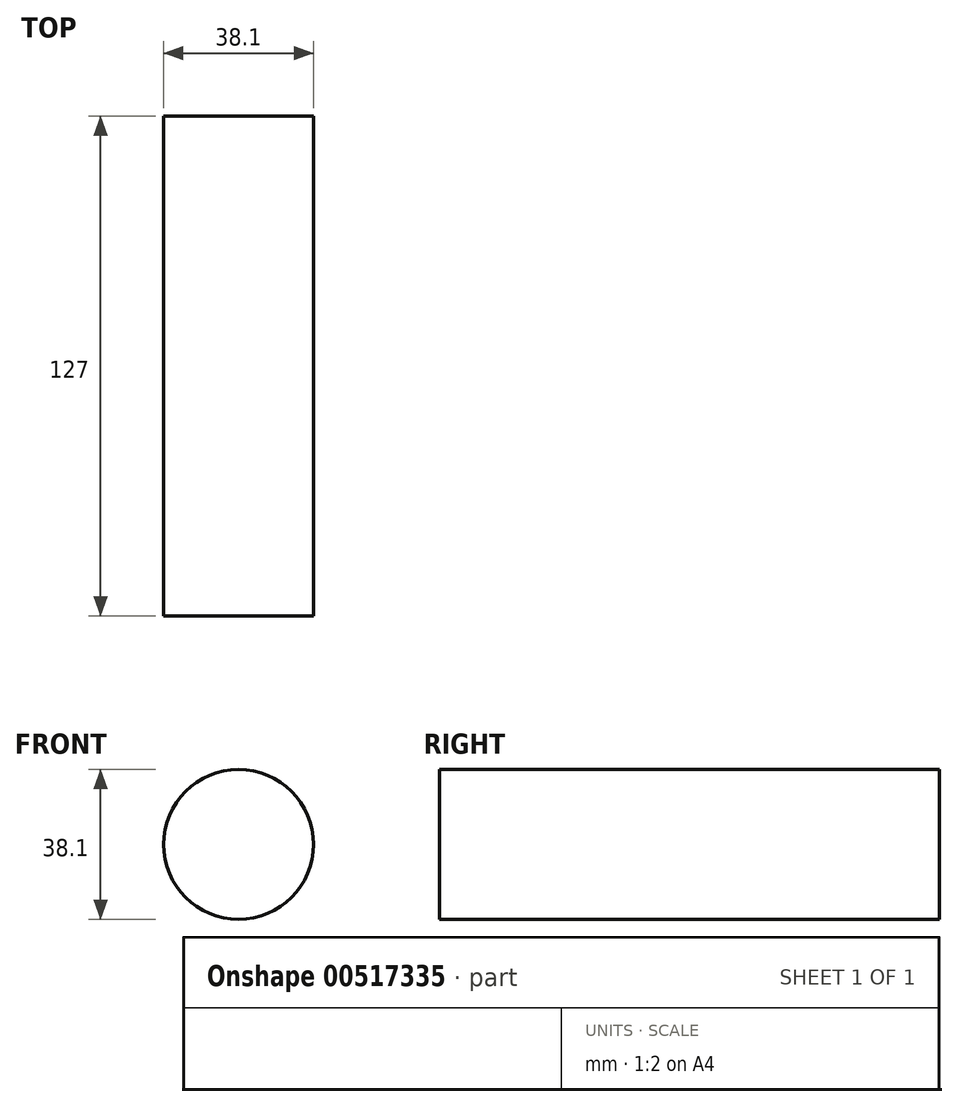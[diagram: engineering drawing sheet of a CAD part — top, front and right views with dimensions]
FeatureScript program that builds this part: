
annotation { "Feature Type Name" : "Feature", "Feature Type Description" : "" }
export const myFeature = defineFeature(function(context is Context, id is Id, definition is map)
    precondition{}
    {
        {
            var Q0;
            Q0=qCreatedBy(makeId("Front.planeOp"),FACE);
            var sketch = newSketch(context, id + "F0", { "sketchPlane" : qUnion([Q0])});
            skCircle(sketch, "E0", {"center": v(0, 0) * mm, "radius": 19.05 * mm});
            skSolve(sketch);
        }
        {
            var Q0;
            Q0=makeQuery(id+"F0.imprint","IMPRINT",FACE,{"disambiguationData":[TD([[makeQuery(id+"F0.imprint","IMPRINT",EDGE,{"derivedFrom":sQuery(id+"F0.wireOp",EDGE,"E0")}),1.0]])]});
            extrude(context, id + "F1", {"entities" : qUnion([Q0]), "endBound" : BoundingType.SYMMETRIC, "depth" : 127 * mm, "offsetDistance" : 25.4 * mm});
        }
    });
